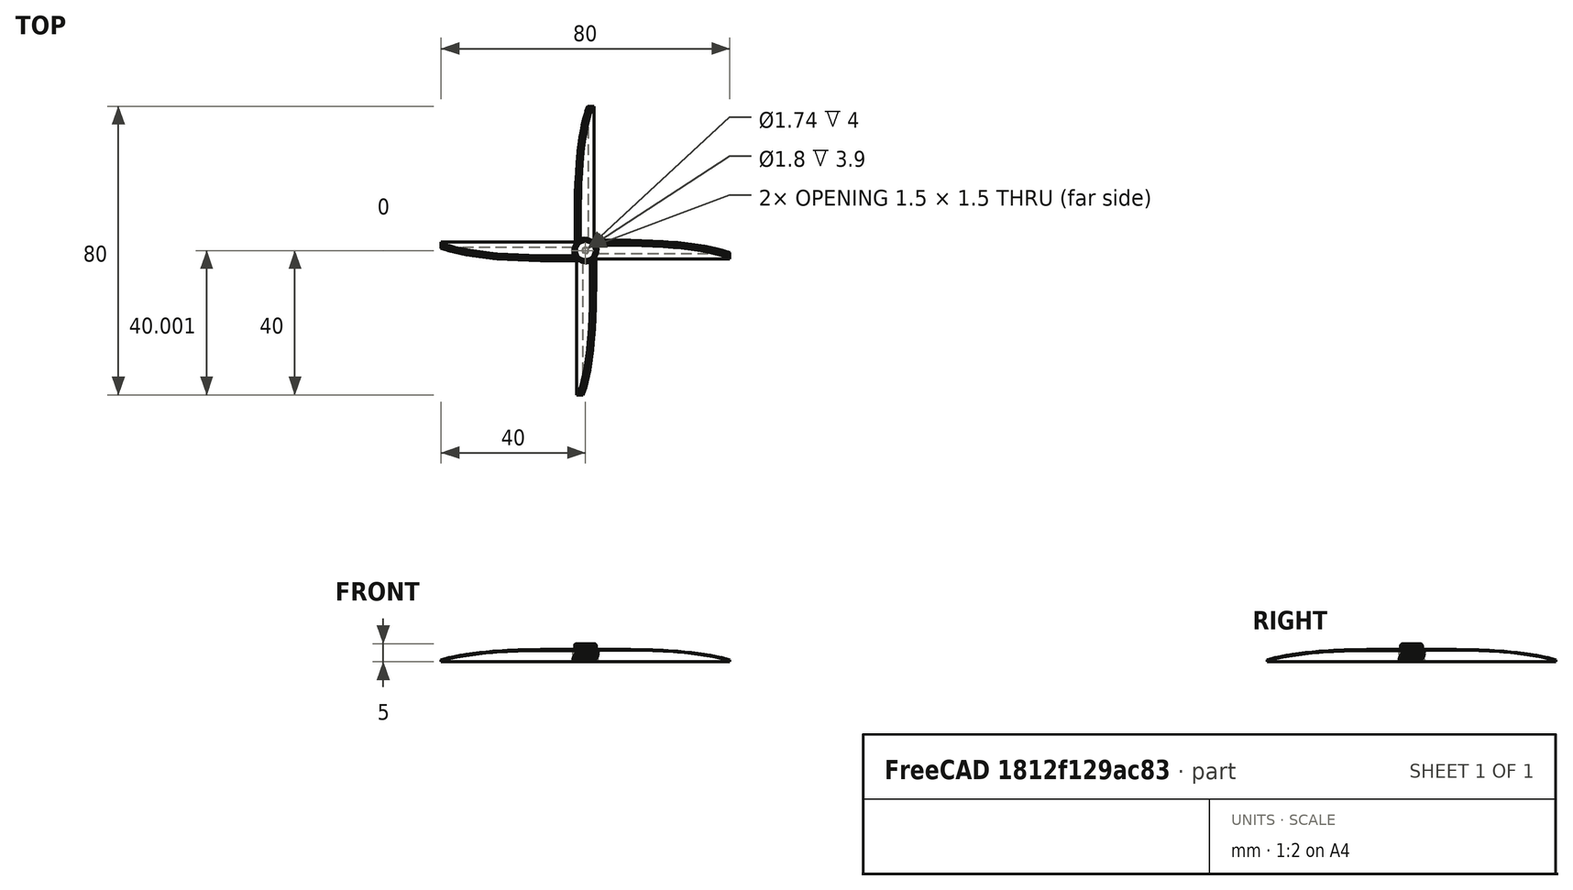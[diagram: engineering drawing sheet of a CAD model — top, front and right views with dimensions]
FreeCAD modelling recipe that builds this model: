
FCSTD DOCUMENT  (FreeCAD 0.18.3R)
Label: Propeller
License: All rights reserved
LicenseURL: http://en.wikipedia.org/wiki/All_rights_reserved
objects: Part::Feature×3, Part::Cylinder×2, Part::Cut×2, Mesh::Feature×1
note: 7 computed .brp shape members not serialized (recipe doc carries the construction recipe); baked Part::Feature solids carry a one-line shape summary decoded from their .brp

FEATURE [Mesh::Feature] Propeller
FEATURE [Part::Feature] Propeller001
  Placement = pos=(0,0,-1.80985) rot=(0,0,1;0rad)
  shape: bbox 80 x 80 x 5 mm, 6258 faces, 0 solids (baked)
FEATURE [Part::Cylinder] Cylinder003
  Angle = 360
  AttacherType = Attacher::AttachEngine3D
  Height = 4
  Placement = pos=(40,40,-0.1) rot=(0,0,1;0rad)
  Radius = 0.9
FEATURE [Part::Feature] Solid
  shape: bbox 80 x 80 x 5 mm, 5861 faces (baked)
FEATURE [Part::Cut] Cut
  Base = -> Solid
  Tool = -> Cylinder003
FEATURE [Part::Feature] Solid001
  shape: bbox 80 x 80 x 5 mm, 5861 faces (baked)
FEATURE [Part::Cylinder] Cylinder004
  Angle = 360
  AttacherType = Attacher::AttachEngine3D
  Height = 4
  Placement = pos=(40,40,0) rot=(0,0,1;0rad)
  Radius = 0.87
FEATURE [Part::Cut] Cut001
  Base = -> Solid001
  Tool = -> Cylinder004
